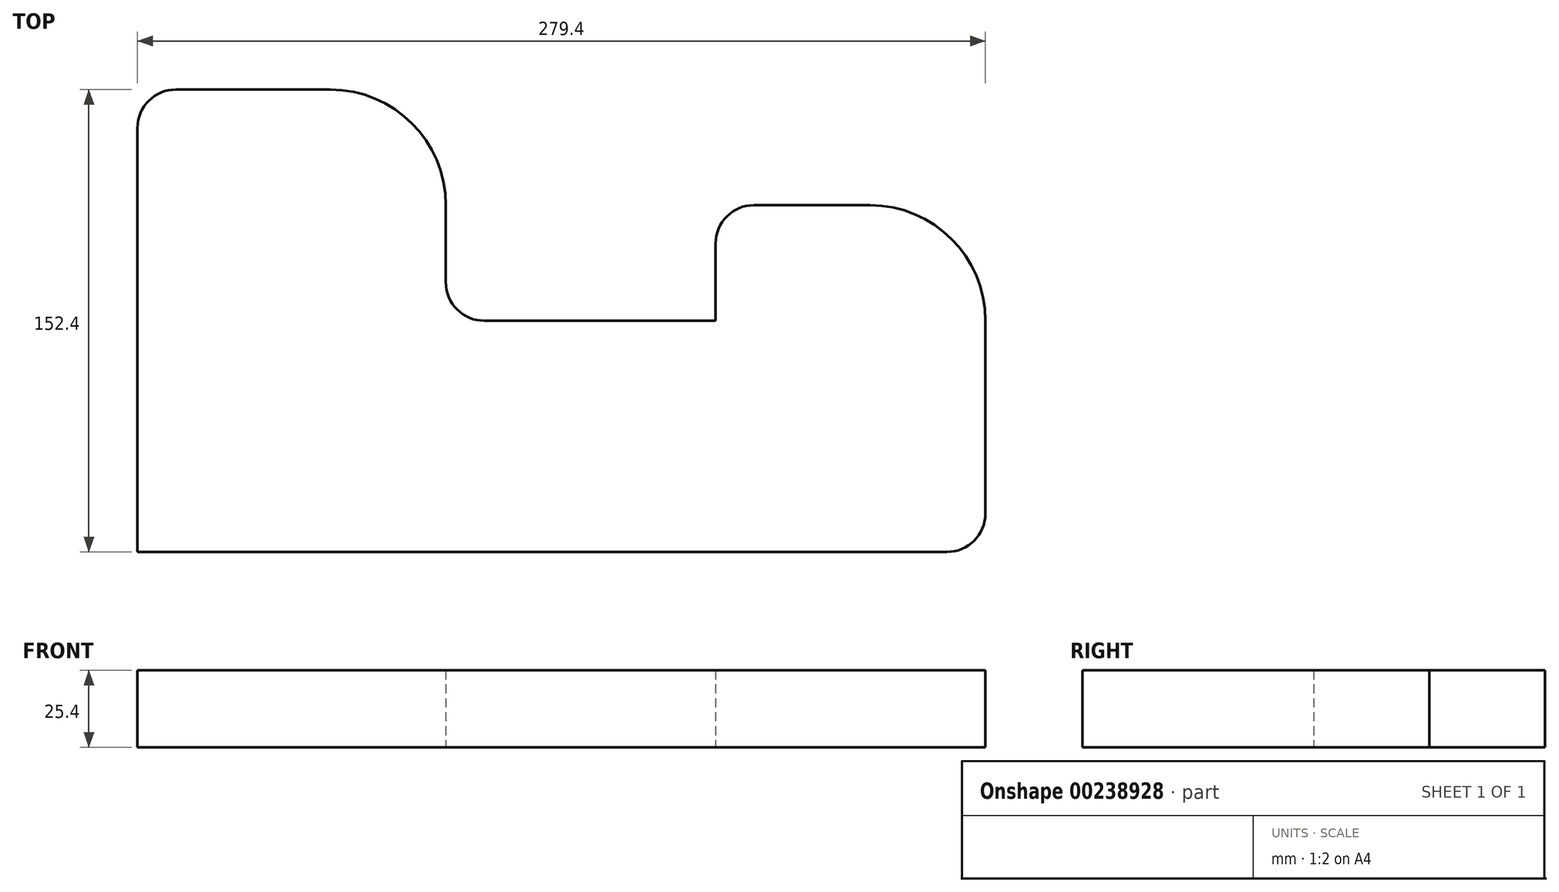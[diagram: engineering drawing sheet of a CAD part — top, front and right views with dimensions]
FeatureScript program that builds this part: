
annotation { "Feature Type Name" : "Feature", "Feature Type Description" : "" }
export const myFeature = defineFeature(function(context is Context, id is Id, definition is map)
    precondition{}
    {
        {
            var Q0;
            Q0=qCreatedBy(makeId("Top.planeOp"),FACE);
            var sketch = newSketch(context, id + "F0", { "sketchPlane" : qUnion([Q0])});
            skLineSegment(sketch, "E0", {"start": v(-114.33, -58.65) * mm, "end": v(152.37, -58.65) * mm});
            skLineSegment(sketch, "E1", {"start": v(165.07, -45.95) * mm, "end": v(165.07, 17.55) * mm});
            skLineSegment(sketch, "E2", {"start": v(126.97, 55.65) * mm, "end": v(88.87, 55.65) * mm});
            skLineSegment(sketch, "E3", {"start": v(76.17, 42.95) * mm, "end": v(76.17, 17.55) * mm});
            skLineSegment(sketch, "E4", {"start": v(76.17, 17.55) * mm, "end": v(-0.03, 17.55) * mm});
            skLineSegment(sketch, "E5", {"start": v(-12.73, 30.25) * mm, "end": v(-12.73, 55.65) * mm});
            skLineSegment(sketch, "E6", {"start": v(-50.83, 93.75) * mm, "end": v(-101.63, 93.75) * mm});
            skLineSegment(sketch, "E7", {"start": v(-114.33, 81.05) * mm, "end": v(-114.33, -58.65) * mm});
            skPoint(sketch, "E8.visualSharp", {"position": v(-114.33, 93.75) * mm});
            skArc(sketch, "E8.filletArc", {"start": v(-101.63, 93.75) * mm, "mid": v(-110.61, 90.03) * mm, "end": v(-114.33, 81.05) * mm});
            skPoint(sketch, "E9.visualSharp", {"position": v(-12.73, 93.75) * mm});
            skArc(sketch, "E9.filletArc", {"start": v(-12.73, 55.65) * mm, "mid": v(-23.9, 82.59) * mm, "end": v(-50.83, 93.75) * mm});
            skPoint(sketch, "E10.visualSharp", {"position": v(-12.73, 17.55) * mm});
            skArc(sketch, "E10.filletArc", {"start": v(-12.73, 30.25) * mm, "mid": v(-9.01, 21.27) * mm, "end": v(-0.03, 17.55) * mm});
            skPoint(sketch, "E11.visualSharp", {"position": v(76.17, 55.65) * mm});
            skArc(sketch, "E11.filletArc", {"start": v(88.87, 55.65) * mm, "mid": v(79.89, 51.93) * mm, "end": v(76.17, 42.95) * mm});
            skPoint(sketch, "E12.visualSharp", {"position": v(165.07, -58.65) * mm});
            skArc(sketch, "E12.filletArc", {"start": v(152.37, -58.65) * mm, "mid": v(161.35, -54.93) * mm, "end": v(165.07, -45.95) * mm});
            skPoint(sketch, "E13.visualSharp", {"position": v(165.07, 55.65) * mm});
            skArc(sketch, "E13.filletArc", {"start": v(165.07, 17.55) * mm, "mid": v(153.9, 44.49) * mm, "end": v(126.97, 55.65) * mm});
            skSolve(sketch);
        }
        {
            var Q0;
            Q0 = qSketchRegion(id + "F0", true);
            extrude(context, id + "F1", {"entities" : qUnion([Q0]), "depth" : 25.4 * mm});
        }
    });
